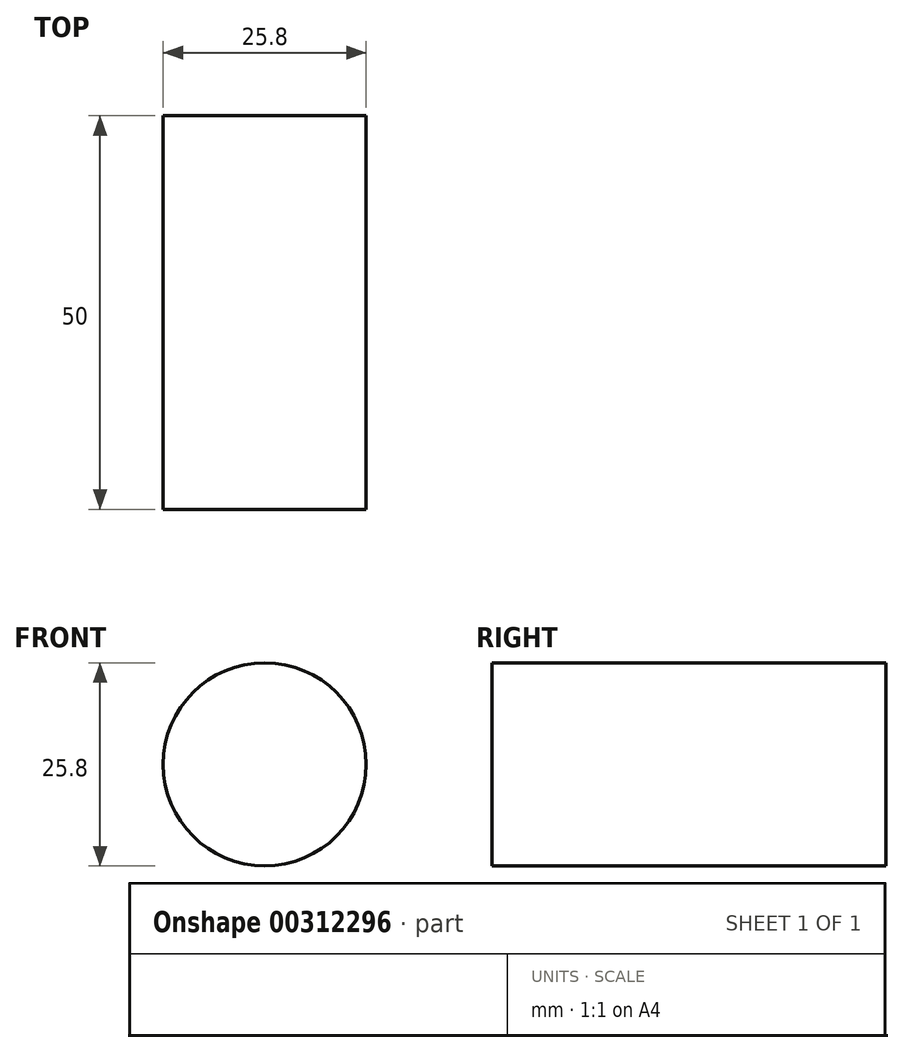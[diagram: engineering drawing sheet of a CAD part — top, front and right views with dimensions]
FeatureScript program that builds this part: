
annotation { "Feature Type Name" : "Feature", "Feature Type Description" : "" }
export const myFeature = defineFeature(function(context is Context, id is Id, definition is map)
    precondition{}
    {
        {
            var Q0;
            Q0=qCreatedBy(makeId("Front.planeOp"),FACE);
            var sketch = newSketch(context, id + "F0", { "sketchPlane" : qUnion([Q0])});
            skCircle(sketch, "E0", {"center": v(0, 0) * mm, "radius": 12.9 * mm});
            skSolve(sketch);
        }
        {
            var Q0;
            Q0=makeQuery(id+"F0.imprint","IMPRINT",FACE,{"disambiguationData":[TD([[makeQuery(id+"F0.imprint","IMPRINT",EDGE,{"derivedFrom":sQuery(id+"F0.wireOp",EDGE,"E0")}),1.0]])]});
            extrude(context, id + "F1", {"entities" : qUnion([Q0]), "oppositeDirection" : true, "depth" : 50 * mm});
        }
    });
